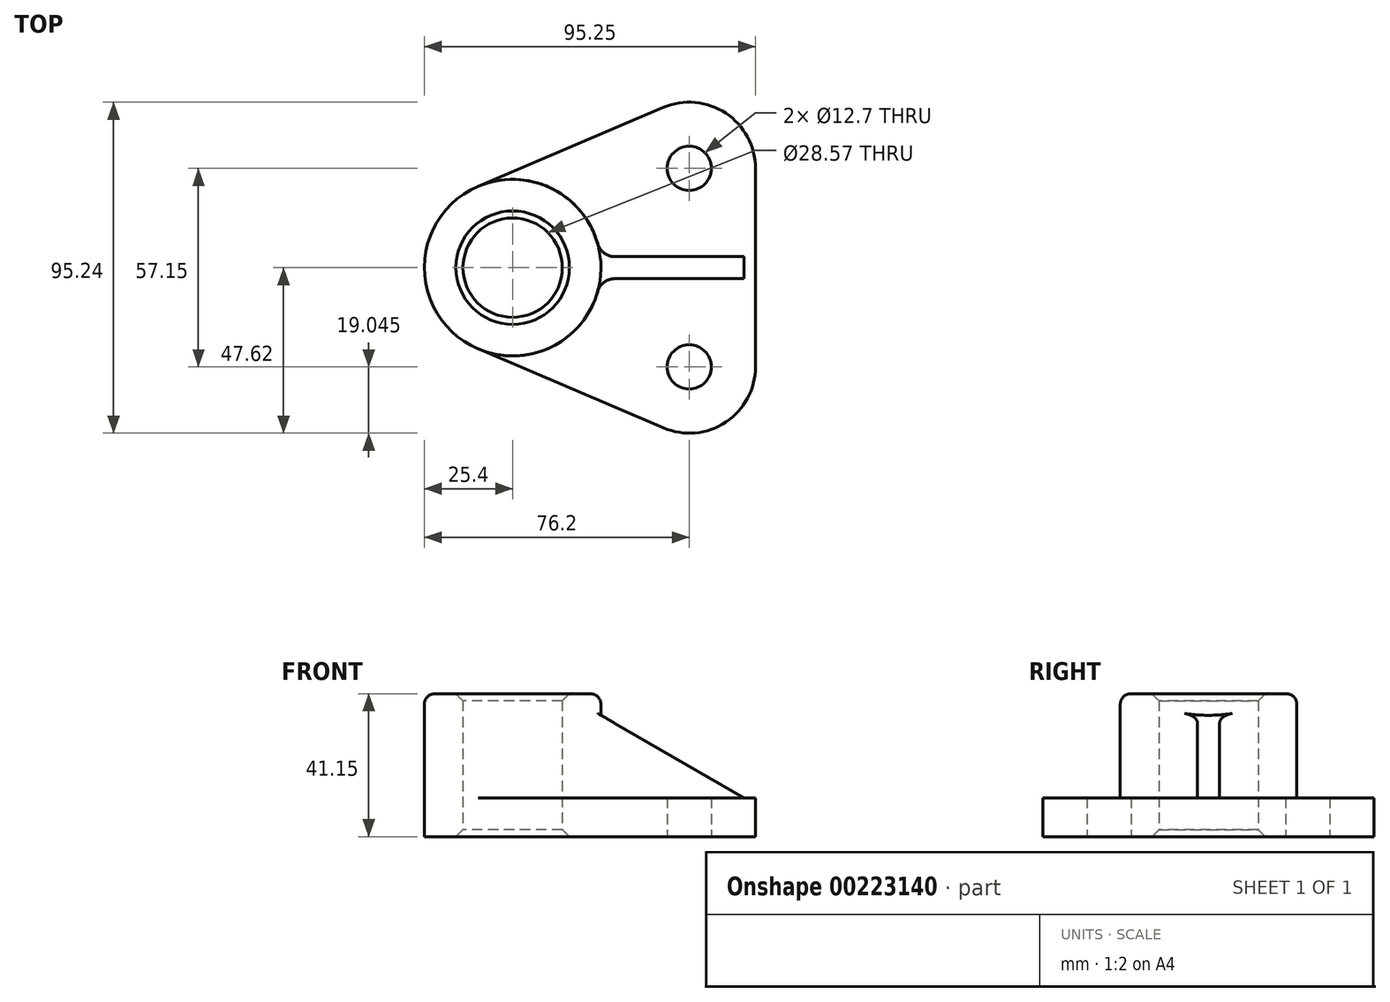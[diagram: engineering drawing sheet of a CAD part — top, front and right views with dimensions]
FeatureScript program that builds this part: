
annotation { "Feature Type Name" : "Feature", "Feature Type Description" : "" }
export const myFeature = defineFeature(function(context is Context, id is Id, definition is map)
    precondition{}
    {
        {
            var Q0;
            Q0=qCreatedBy(makeId("Top.planeOp"),FACE);
            var sketch = newSketch(context, id + "F0", { "sketchPlane" : qUnion([Q0])});
            skArc(sketch, "E0", {"start": v(25.4, 0) * mm, "mid": v(0, 25.4) * mm, "end": v(-25.4, 0) * mm});
            skArc(sketch, "E1", {"start": v(14.29, 0) * mm, "mid": v(0, 14.29) * mm, "end": v(-14.29, 0) * mm});
            skCircle(sketch, "E2", {"center": v(50.8, 28.57) * mm, "radius": 6.35 * mm});
            skArc(sketch, "E3", {"start": v(69.85, 28.57) * mm, "mid": v(61.3, 44.47) * mm, "end": v(43.33, 46.1) * mm});
            skLineSegment(sketch, "E4", {"start": v(-9.97, 23.36) * mm, "end": v(43.33, 46.1) * mm});
            skLineSegment(sketch, "E5", {"start": v(69.85, 28.57) * mm, "end": v(69.85, 0) * mm});
            skLineSegment(sketch, "E6", {"start": v(-25.4, 0) * mm, "end": v(69.85, 0) * mm, "construction": true});
            skLineSegment(sketch, "E7.MirrorCS", {"start": v(69.85, -28.58) * mm, "end": v(69.85, 0) * mm});
            skArc(sketch, "E8.MirrorCS", {"start": v(69.85, -28.58) * mm, "mid": v(61.3, -44.47) * mm, "end": v(43.33, -46.1) * mm});
            skCircle(sketch, "E9.MirrorC", {"center": v(50.8, -28.58) * mm, "radius": 6.35 * mm});
            skLineSegment(sketch, "E10.MirrorCS", {"start": v(-9.97, -23.36) * mm, "end": v(43.33, -46.1) * mm});
            skArc(sketch, "E11.MirrorCS", {"start": v(25.4, 0) * mm, "mid": v(0, -25.4) * mm, "end": v(-25.4, 0) * mm});
            skArc(sketch, "E12.MirrorCS", {"start": v(14.29, 0) * mm, "mid": v(0, -14.29) * mm, "end": v(-14.29, 0) * mm});
            skSolve(sketch);
        }
        {
            var Q0;
            Q0=makeQuery(id+"F0.imprint","IMPRINT",FACE,{"disambiguationData":[TD([[makeQuery(id+"F0.imprint","IMPRINT",EDGE,{"derivedFrom":sQuery(id+"F0.wireOp",EDGE,"E2")}),-1.0]])]});
            extrude(context, id + "F1", {"entities" : qUnion([Q0]), "depth" : 11.18 * mm});
        }
        {
            var Q0;
            Q0=makeQuery(id+"F0.imprint","IMPRINT",FACE,{"disambiguationData":[TD([[makeQuery(id+"F0.imprint","IMPRINT",EDGE,{"derivedFrom":sQuery(id+"F0.wireOp",EDGE,"E1")}),-1.0]])]});
            extrude(context, id + "F2", {"entities" : qUnion([Q0]), "operationType" : NewBodyOperationType.ADD, "depth" : 41.15 * mm});
        }
        {
            var Q0;
            Q0=qCreatedBy(makeId("Front.planeOp"),FACE);
            var sketch = newSketch(context, id + "F3", { "sketchPlane" : qUnion([Q0])});
            skLineSegment(sketch, "E13.0", {"start": v(69.85, 11.18) * mm, "end": v(43.33, 11.18) * mm});
            skLineSegment(sketch, "E14", {"start": v(69.85, 11.18) * mm, "end": v(66.55, 11.18) * mm});
            skLineSegment(sketch, "E15", {"start": v(66.55, 11.18) * mm, "end": v(22.55, 36.58) * mm});
            skLineSegment(sketch, "E16", {"start": v(43.33, 11.18) * mm, "end": v(22.55, 11.18) * mm});
            skLineSegment(sketch, "E17", {"start": v(22.55, 36.58) * mm, "end": v(22.55, 11.18) * mm});
            skSolve(sketch);
        }
        {
            var Q0;
            Q0 = qSketchRegion(id + "F3", true);
            extrude(context, id + "F4", {"entities" : qUnion([Q0]), "operationType" : NewBodyOperationType.ADD, "endBound" : BoundingType.SYMMETRIC, "depth" : 6.35 * mm});
        }
        {
            var Q0;
            Q0=makeQuery(id+"F2.opExtrude","CAP_EDGE",EDGE,{"disambiguationData":[OSD([sQuery(id+"F0.wireOp",EDGE,"E0"),sQuery(id+"F0.wireOp",EDGE,"E11.MirrorCS")])],"isStart":false});
            fillet(context, id + "F5", {"entities" : qUnion([Q0]), "radius" : 3.05 * mm, "tangentPropagation" : true, "allowEdgeOverflow" : false});
        }
        {
            var Q0;
            {var subQ0=sQuery(id+"F0.wireOp",EDGE,"E11.MirrorCS");var subQ1=sQuery(id+"F0.wireOp",EDGE,"E10.MirrorCS");var subQ2=sQuery(id+"F0.wireOp",EDGE,"E0");Q0=makeQuery(id+"F4.boolean.opBoolean","SPLIT",EDGE,{"disambiguationData":[TD([makeQuery(id+"F1.opExtrude","SWEPT_FACE",FACE,{"disambiguationData":[OSD([subQ1])]})])],"derivedFrom":makeQuery(id+"F1.opExtrude","CAP_EDGE",EDGE,{"disambiguationData":[OSD([subQ2,subQ0])],"isStart":false})});}
            var Q1;
            {var subQ0=sQuery(id+"F0.wireOp",EDGE,"E11.MirrorCS");var subQ1=sQuery(id+"F0.wireOp",EDGE,"E4");var subQ2=sQuery(id+"F0.wireOp",EDGE,"E0");Q1=makeQuery(id+"F4.boolean.opBoolean","SPLIT",EDGE,{"disambiguationData":[TD([makeQuery(id+"F1.opExtrude","SWEPT_FACE",FACE,{"disambiguationData":[OSD([subQ1])]})])],"derivedFrom":makeQuery(id+"F1.opExtrude","CAP_EDGE",EDGE,{"disambiguationData":[OSD([subQ2,subQ0])],"isStart":false})});}
            var Q2;
            Q2=makeQuery(id+"F4.opExtrude","CAP_EDGE",EDGE,{"disambiguationData":[OSD([sQuery(id+"F3.wireOp",EDGE,"E13.0"),sQuery(id+"F3.wireOp",EDGE,"E16")])],"isStart":false});
            var Q3;
            Q3=makeQuery(id+"F4.boolean.opBoolean","INTERSECT",EDGE,{"derivedFrom":[makeQuery(id+"F2.opExtrude","SWEPT_FACE",FACE,{"disambiguationData":[OSD([sQuery(id+"F0.wireOp",EDGE,"E0"),sQuery(id+"F0.wireOp",EDGE,"E11.MirrorCS")])]}),makeQuery(id+"F4.opExtrude","CAP_FACE",FACE,{"disambiguationData":[OSD([sQuery(id+"F3.wireOp",EDGE,"E13.0"),sQuery(id+"F3.wireOp",EDGE,"E15"),sQuery(id+"F3.wireOp",EDGE,"E16"),sQuery(id+"F3.wireOp",EDGE,"E17")])],"isStart":false})]});
            var Q4;
            Q4=makeQuery(id+"F4.boolean.opBoolean","INTERSECT",EDGE,{"derivedFrom":[makeQuery(id+"F2.opExtrude","SWEPT_FACE",FACE,{"disambiguationData":[OSD([sQuery(id+"F0.wireOp",EDGE,"E0"),sQuery(id+"F0.wireOp",EDGE,"E11.MirrorCS")])]}),makeQuery(id+"F4.opExtrude","CAP_FACE",FACE,{"disambiguationData":[OSD([sQuery(id+"F3.wireOp",EDGE,"E13.0"),sQuery(id+"F3.wireOp",EDGE,"E15"),sQuery(id+"F3.wireOp",EDGE,"E16"),sQuery(id+"F3.wireOp",EDGE,"E17")])],"isStart":true})]});
            var Q5;
            Q5=makeQuery(id+"F4.opExtrude","CAP_EDGE",EDGE,{"disambiguationData":[OSD([sQuery(id+"F3.wireOp",EDGE,"E13.0"),sQuery(id+"F3.wireOp",EDGE,"E16")])],"isStart":true});
            fillet(context, id + "F6", {"entities" : qUnion([Q0, Q1, Q2, Q3, Q4, Q5]), "radius" : 5.08 * mm, "tangentPropagation" : true, "allowEdgeOverflow" : false});
        }
        {
            var Q0;
            Q0=makeQuery(id+"F2.opExtrude","CAP_EDGE",EDGE,{"disambiguationData":[OSD([sQuery(id+"F0.wireOp",EDGE,"E1"),sQuery(id+"F0.wireOp",EDGE,"E12.MirrorCS")])],"isStart":false});
            var Q1;
            Q1=makeQuery(id+"F2.opExtrude","CAP_EDGE",EDGE,{"disambiguationData":[OSD([sQuery(id+"F0.wireOp",EDGE,"E1"),sQuery(id+"F0.wireOp",EDGE,"E12.MirrorCS")])],"isStart":true});
            chamfer(context, id + "F7", {"entities" : qUnion([Q0, Q1]), "chamferType" : ChamferType.OFFSET_ANGLE, "width" : 2.03 * mm, "oppositeDirection" : false, "angle" : 45 * degree, "tangentPropagation" : true});
        }
    });
